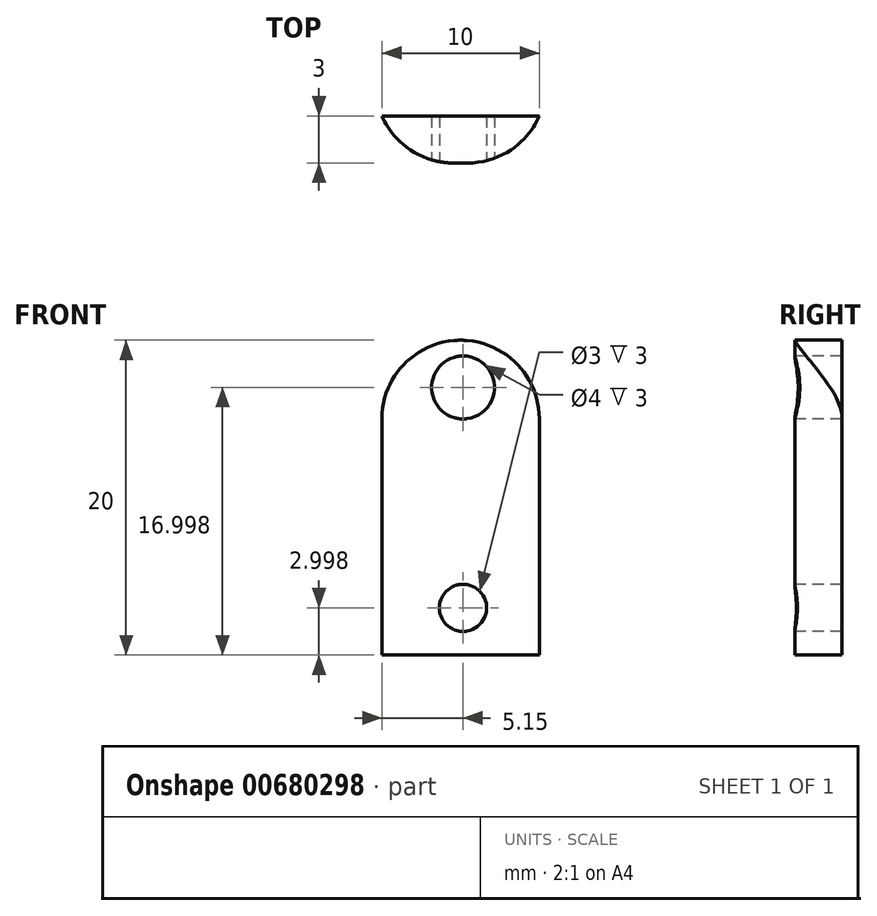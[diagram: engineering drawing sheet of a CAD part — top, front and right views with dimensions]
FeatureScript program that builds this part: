
annotation { "Feature Type Name" : "Feature", "Feature Type Description" : "" }
export const myFeature = defineFeature(function(context is Context, id is Id, definition is map)
    precondition{}
    {
        {
            var Q0;
            Q0=qCreatedBy(makeId("Front.planeOp"),FACE);
            var sketch = newSketch(context, id + "F0", { "sketchPlane" : qUnion([Q0])});
            skLineSegment(sketch, "E0", {"start": v(4.85, 10.15) * mm, "end": v(4.85, -9.85) * mm});
            skLineSegment(sketch, "E1", {"start": v(-5.15, -9.85) * mm, "end": v(-5.15, 10.15) * mm});
            skLineSegment(sketch, "E2", {"start": v(-5.15, 10.15) * mm, "end": v(4.85, 10.15) * mm});
            skLineSegment(sketch, "E3", {"start": v(-5.15, -9.85) * mm, "end": v(4.85, -9.85) * mm});
            skSolve(sketch);
        }
        {
            var Q0;
            Q0 = qSketchRegion(id + "F0", true);
            extrude(context, id + "F1", {"entities" : qUnion([Q0]), "depth" : 3 * mm, "offsetDistance" : 25 * mm});
        }
        {
            var Q0;
            Q0=makeQuery(id+"F1.opExtrude","CAP_FACE",FACE,{"disambiguationData":[OSD([sQuery(id+"F0.wireOp",EDGE,"E0"),sQuery(id+"F0.wireOp",EDGE,"E1"),sQuery(id+"F0.wireOp",EDGE,"E2"),sQuery(id+"F0.wireOp",EDGE,"E3")])],"isStart":false});
            var sketch = newSketch(context, id + "F2", { "sketchPlane" : qUnion([Q0])});
            skPoint(sketch, "E4", {"position": v(0, 10.15) * mm});
            skPoint(sketch, "E5", {"position": v(0, 7.15) * mm});
            skCircle(sketch, "E6", {"center": v(0, 7.15) * mm, "radius": 2 * mm});
            skPoint(sketch, "E7", {"position": v(0, -9.85) * mm});
            skPoint(sketch, "E8", {"position": v(0, -6.85) * mm});
            skCircle(sketch, "E9", {"center": v(0, -6.85) * mm, "radius": 1.5 * mm});
            skSolve(sketch);
        }
        {
            var Q0;
            Q0 = qSketchRegion(id + "F2", true);
            extrude(context, id + "F3", {"entities" : qUnion([Q0]), "operationType" : NewBodyOperationType.REMOVE, "endBound" : BoundingType.THROUGH_ALL, "oppositeDirection" : true, "depth" : 25 * mm, "offsetDistance" : 25 * mm});
        }
        {
            var Q0;
            Q0=makeQuery(id+"F1.opExtrude","SWEPT_EDGE",EDGE,{"disambiguationData":[OSD([sQuery(id+"F0.wireOp",EDGE,"E0"),sQuery(id+"F0.wireOp",EDGE,"E2")])]});
            var Q1;
            Q1=makeQuery(id+"F1.opExtrude","SWEPT_EDGE",EDGE,{"disambiguationData":[OSD([sQuery(id+"F0.wireOp",EDGE,"E1"),sQuery(id+"F0.wireOp",EDGE,"E2")])]});
            var Q2;
            Q2=makeQuery(id+"F1.opExtrude","CAP_EDGE",EDGE,{"disambiguationData":[OSD([sQuery(id+"F0.wireOp",EDGE,"E1")])],"isStart":false});
            var Q3;
            Q3=makeQuery(id+"F1.opExtrude","CAP_EDGE",EDGE,{"disambiguationData":[OSD([sQuery(id+"F0.wireOp",EDGE,"E0")])],"isStart":false});
            fillet(context, id + "F4", {"entities" : qUnion([Q0, Q1, Q2, Q3]), "radius" : 5 * mm, "tangentPropagation" : true, "allowEdgeOverflow" : false});
        }
    });
